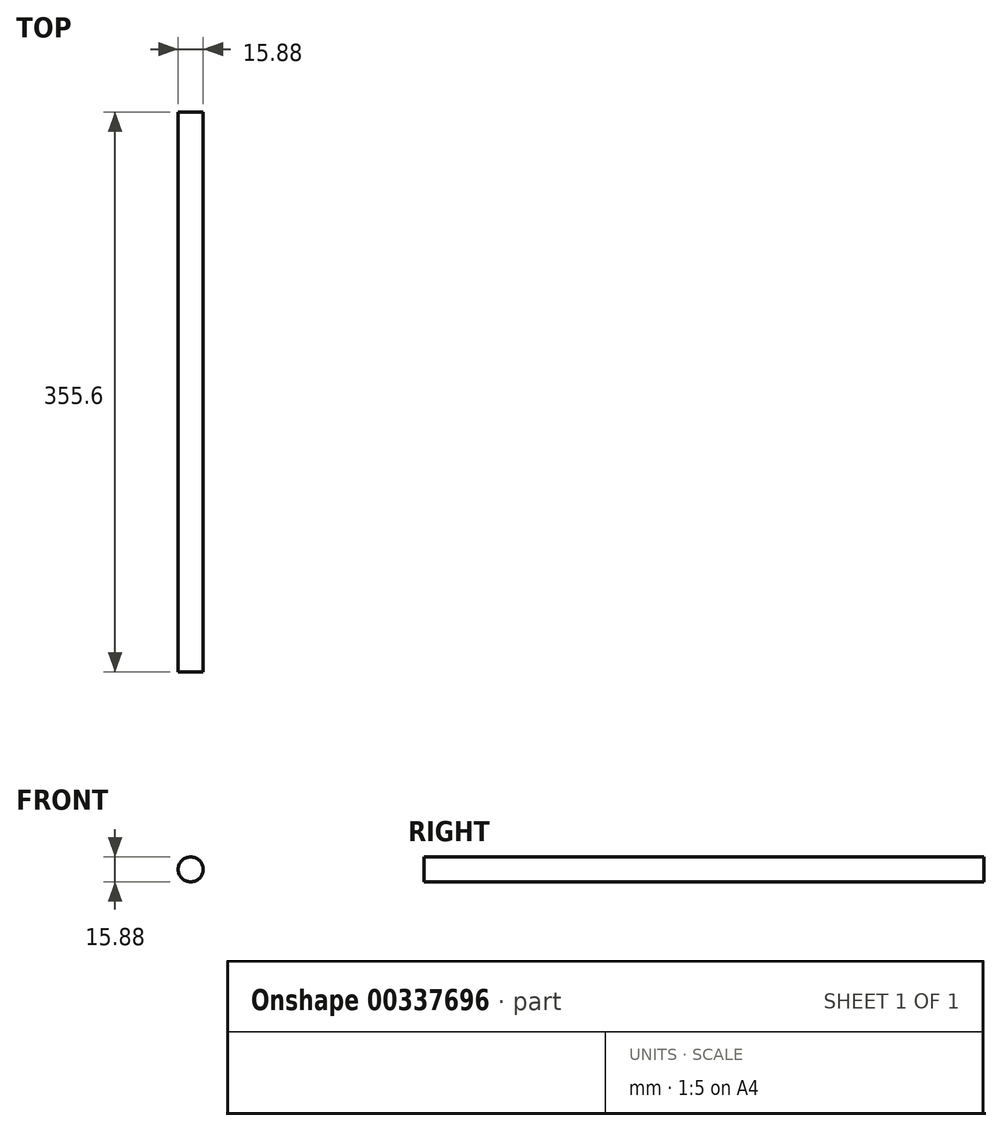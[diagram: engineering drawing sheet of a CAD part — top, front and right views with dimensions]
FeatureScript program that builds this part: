
annotation { "Feature Type Name" : "Feature", "Feature Type Description" : "" }
export const myFeature = defineFeature(function(context is Context, id is Id, definition is map)
    precondition{}
    {
        {
            var Q0;
            Q0=qCreatedBy(makeId("Front.planeOp"),FACE);
            var sketch = newSketch(context, id + "F0", { "sketchPlane" : qUnion([Q0])});
            skCircle(sketch, "E0", {"center": v(0, 0) * mm, "radius": 7.94 * mm});
            skSolve(sketch);
        }
        {
            var Q0;
            Q0 = qSketchRegion(id + "F0", true);
            extrude(context, id + "F1", {"entities" : qUnion([Q0]), "endBound" : BoundingType.SYMMETRIC, "depth" : 355.6 * mm});
        }
    });
